# Revit family: Haworth_Cappellini_HiPad_Stool_EU_PRELIMINARY
name_source: partatom
category: Furniture
revit_build: Autodesk Revit 2018 (Build: 20170223_1515(x64)
units: mm (PartAtom-declared; Revit-internal decimal feet)

## family parameters
Always vertical = Yes
Cut with Voids When Loaded = No
OmniClass Number = 23.40.70.14.64.21
OmniClass Title = Systems Furniture
Room Calculation Point = No
Shared = No
Work Plane-Based = No

## types (3) — shared parameters
Actual Depth = 35 cm
Actual Width = 44 cm
Assembly Code = E2020200
Description = Haworth - Cappellini - Hi-Pad - Stool
Glide Finish = Haworth _ Polymer _ Black
Manufacturer = Haworth
Model = HP_1X
Revision Number = 8
Size = Verify Final Dim. w/ Haworth
URL = https://www.haworth.com
URL - Product = https://www.haworth.com
Warranty = http://www.haworth.com

## per-type parameters (varying)
| type | Actual Height | Bar Height | High | Low | Medium | Seat Height Offset |
| High Stool | 80 cm | 38 cm | Yes | No | No | 71 cm |
| Medium Stool | 70 cm | 28 cm | No | No | Yes | 61 cm |
| Low Stool | 45 cm | 28 cm | No | Yes | No | 38 cm |

## geometry (parser evidence)
native form markers: Sweep x6
no freeform markers — native parametric forms only
